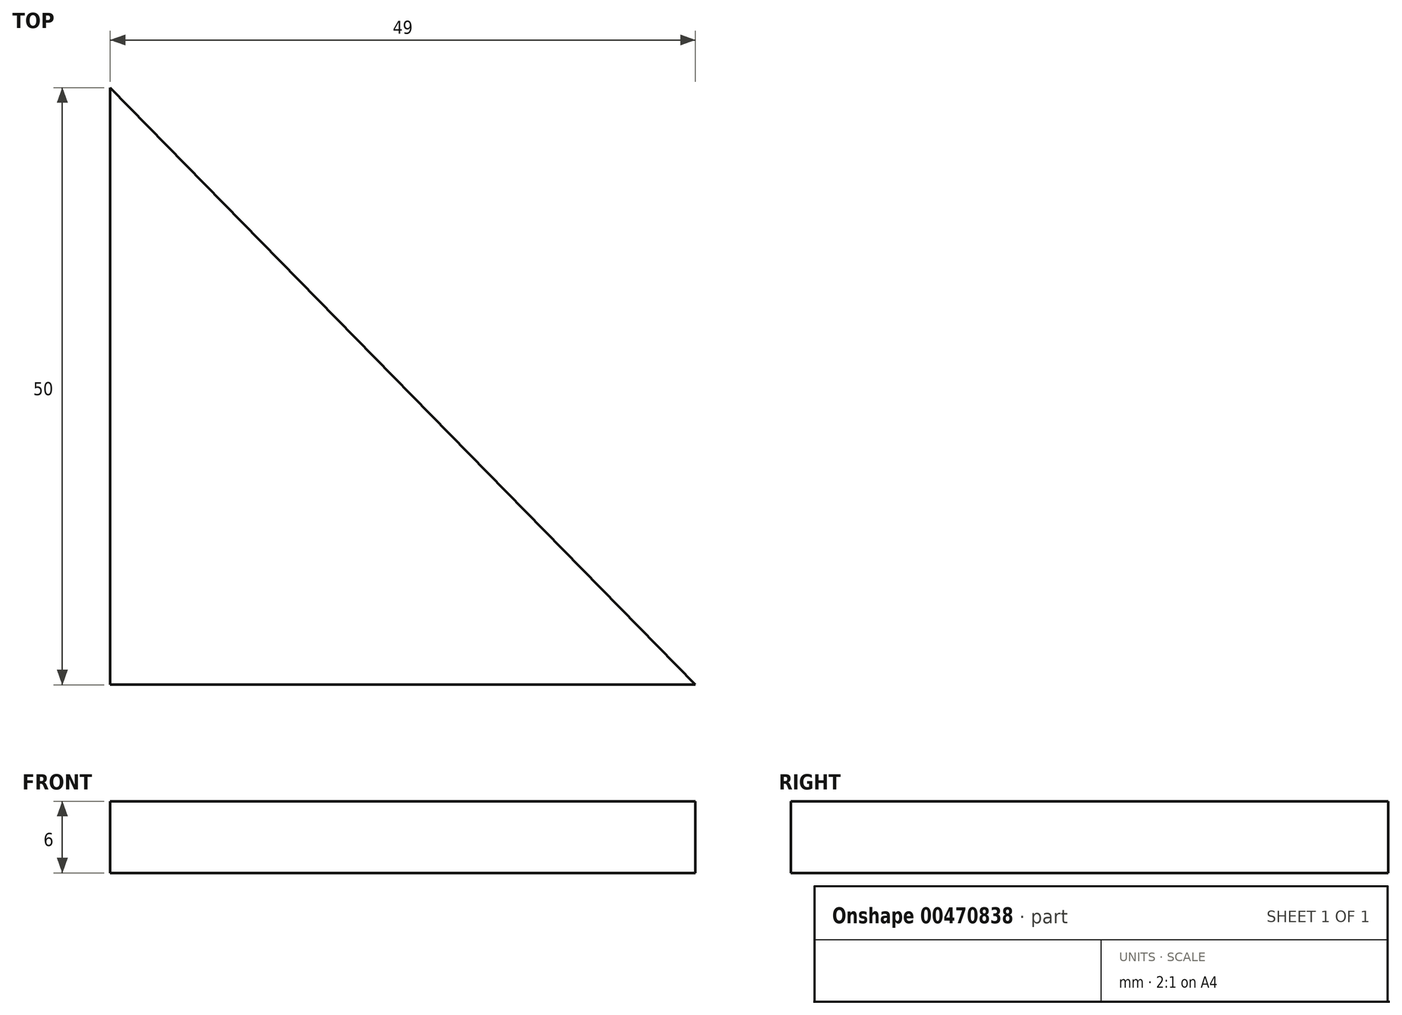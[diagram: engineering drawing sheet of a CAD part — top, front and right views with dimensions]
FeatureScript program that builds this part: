
annotation { "Feature Type Name" : "Feature", "Feature Type Description" : "" }
export const myFeature = defineFeature(function(context is Context, id is Id, definition is map)
    precondition{}
    {
        {
            var Q0;
            Q0=qCreatedBy(makeId("Top.planeOp"),FACE);
            var sketch = newSketch(context, id + "F0", { "sketchPlane" : qUnion([Q0])});
            skLineSegment(sketch, "E0", {"start": v(-28.95, 122.6) * mm, "end": v(-28.95, 72.6) * mm});
            skLineSegment(sketch, "E1", {"start": v(-28.95, 72.6) * mm, "end": v(20.05, 72.6) * mm});
            skLineSegment(sketch, "E2", {"start": v(-28.95, 122.6) * mm, "end": v(20.05, 72.6) * mm});
            skSolve(sketch);
        }
        {
            var Q0;
            Q0=makeQuery(id+"F0.imprint","IMPRINT",FACE,{"disambiguationData":[TD([[makeQuery(id+"F0.imprint","IMPRINT",EDGE,{"derivedFrom":sQuery(id+"F0.wireOp",EDGE,"E0")}),1.0]])]});
            extrude(context, id + "F1", {"entities" : qUnion([Q0]), "depth" : 6 * mm});
        }
    });
